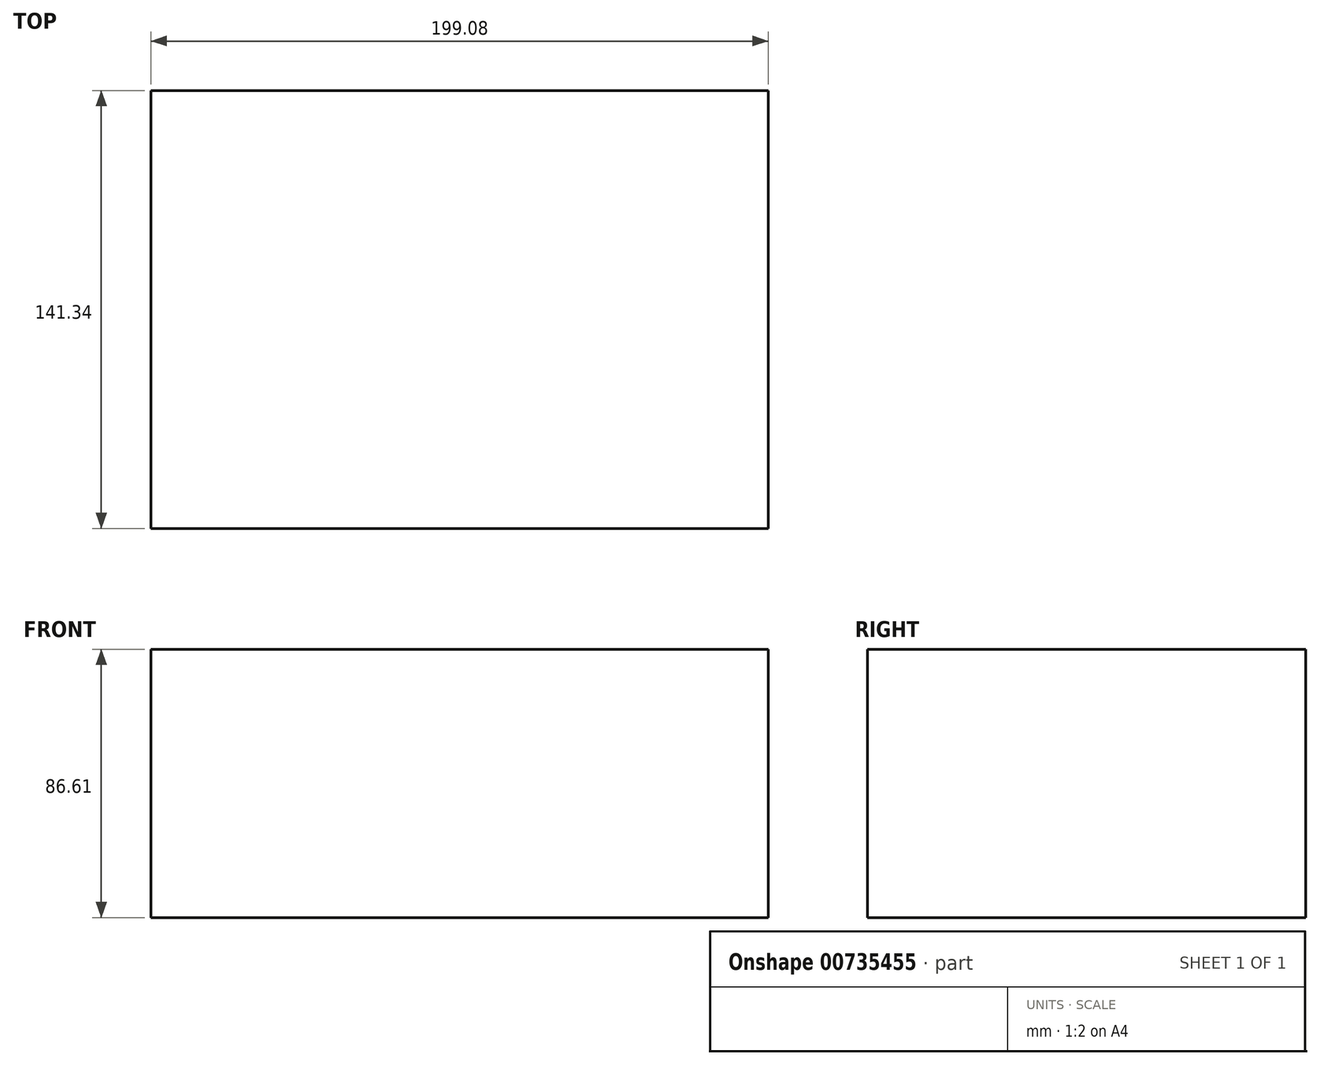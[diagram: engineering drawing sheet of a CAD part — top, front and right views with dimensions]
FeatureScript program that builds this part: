
annotation { "Feature Type Name" : "Feature", "Feature Type Description" : "" }
export const myFeature = defineFeature(function(context is Context, id is Id, definition is map)
    precondition{}
    {
        {
            var Q0;
            Q0=qCreatedBy(makeId("Top.planeOp"),FACE);
            var sketch = newSketch(context, id + "F0", { "sketchPlane" : qUnion([Q0])});
            skLineSegment(sketch, "E0.bottom", {"start": v(99.54, 70.67) * mm, "end": v(-99.54, 70.67) * mm});
            skLineSegment(sketch, "E0.top", {"start": v(99.54, -70.67) * mm, "end": v(-99.54, -70.67) * mm});
            skLineSegment(sketch, "E0.left", {"start": v(99.54, 70.67) * mm, "end": v(99.54, -70.67) * mm});
            skLineSegment(sketch, "E0.right", {"start": v(-99.54, 70.67) * mm, "end": v(-99.54, -70.67) * mm});
            skPoint(sketch, "E0.middle", {"position": v(0, 0) * mm});
            skSolve(sketch);
        }
        {
            var Q0;
            Q0=makeQuery(id+"F0.imprint","IMPRINT",FACE,{"disambiguationData":[TD([[makeQuery(id+"F0.imprint","IMPRINT",EDGE,{"derivedFrom":sQuery(id+"F0.wireOp",EDGE,"E0.bottom")}),1.0]])]});
            extrude(context, id + "F1", {"entities" : qUnion([Q0]), "depth" : 86.61 * mm, "offsetDistance" : 25.4 * mm});
        }
    });
